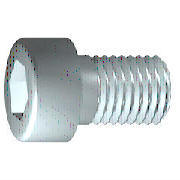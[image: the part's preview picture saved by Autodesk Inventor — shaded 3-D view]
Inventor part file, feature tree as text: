
AUTODESK INVENTOR PART (.ipt)
format: ipt  version: 2025.1 (Build 291241000, 241)  size: 197,120 bytes
history: native  units: mm (DEFAULTED — no unit token found)
features: other x1, extrude x1, plane x1, fillet x1
ambient origin geometry x7: Origin, YZ Plane, XY Plane, X Axis, Y Axis, Z Axis, Center Point
bodies: Solid1 (feature_tree)
feature tree (4):
  other  "Corps"
  extrude  "Rainure"  Depth=4.0mm
  plane  "Work Plane1"
  fillet  "Fillet2"  Radius=0.24548mm
